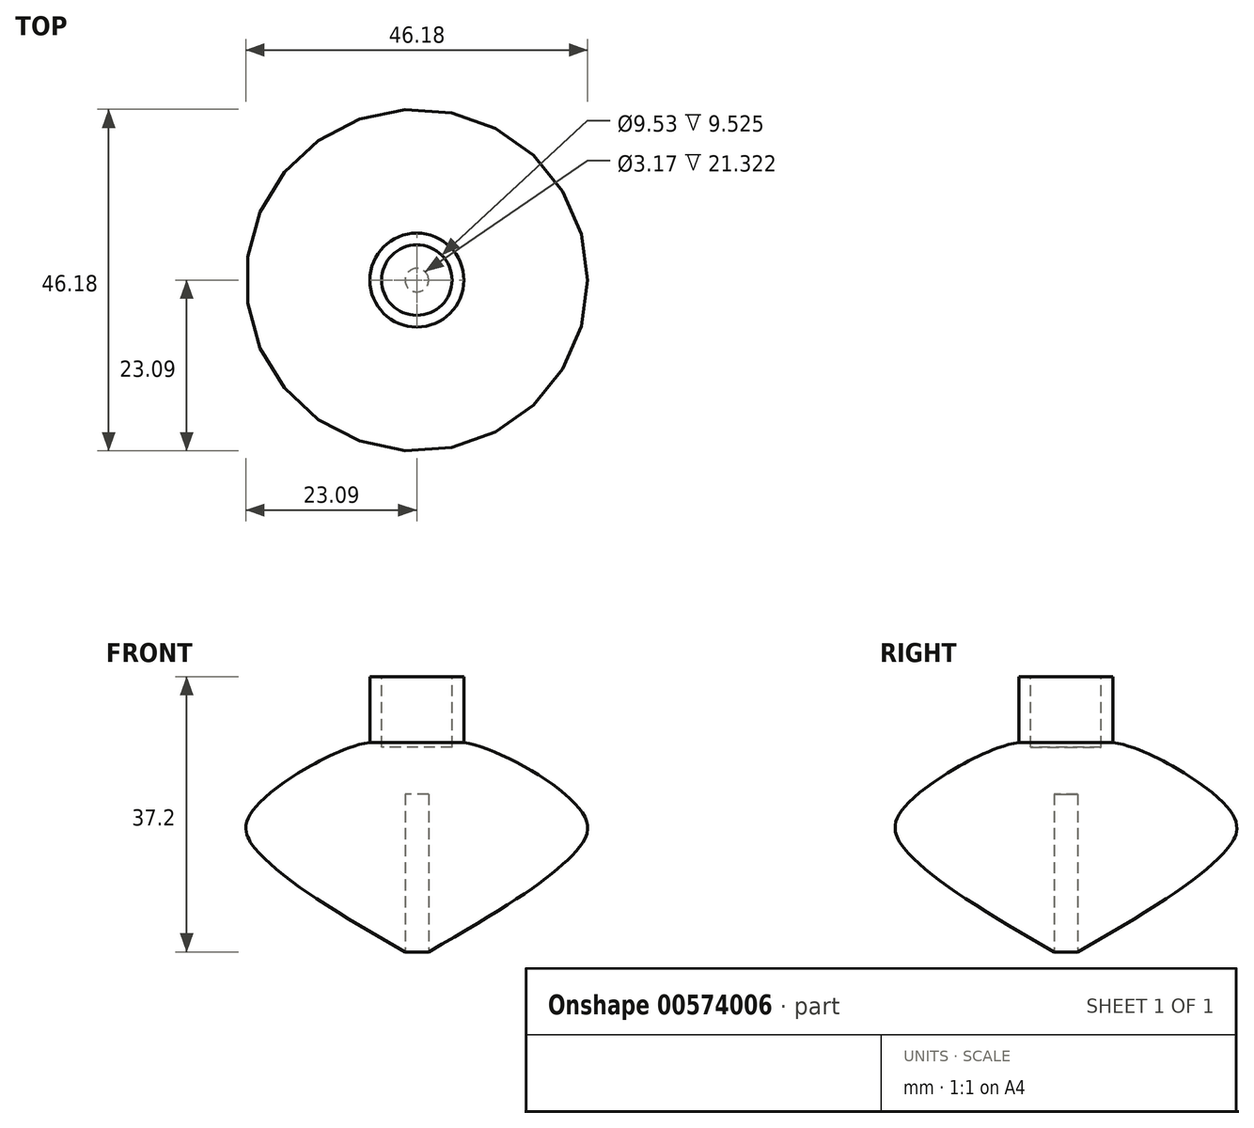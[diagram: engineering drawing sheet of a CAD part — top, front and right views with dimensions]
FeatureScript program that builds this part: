
annotation { "Feature Type Name" : "Feature", "Feature Type Description" : "" }
export const myFeature = defineFeature(function(context is Context, id is Id, definition is map)
    precondition{}
    {
        {
            var Q0;
            Q0=qCreatedBy(makeId("Front.planeOp"),FACE);
            var sketch = newSketch(context, id + "F0", { "sketchPlane" : qUnion([Q0])});
            skFitSpline(sketch, "E0", {"points": [v(0, 0) * mm, v(21.22, 14.16) * mm, v(22.56, 19.42) * mm, v(6.35, 29.21) * mm], "startDerivative": vector(81.94, 46.46) * mm, "endDerivative": vector(-34.66, 4.34) * mm});
            skLineSegment(sketch, "E1", {"start": v(6.35, 29.21) * mm, "end": v(6.35, 38.1) * mm});
            skLineSegment(sketch, "E2", {"start": v(6.35, 38.1) * mm, "end": v(0, 38.1) * mm});
            skLineSegment(sketch, "E3", {"start": v(0, 38.1) * mm, "end": v(0, 0) * mm});
            skLineSegment(sketch, "E4", {"start": v(23.08, 17.5) * mm, "end": v(23.08, 9.82) * mm});
            skSolve(sketch);
        }
        {
            var Q0;
            Q0=qSketchRegion(id+"F0",true);
            var Q1;
            Q1=sQuery(id+"F0.wireOp",EDGE,"E3");
            revolve(context, id + "F1", {"entities" : qUnion([Q0]), "axis" : qUnion([Q1]), "revolveType" : RevolveType.FULL});
        }
        {
            var Q0;
            Q0=makeQuery(id+"F1.opRevolve","SWEPT_FACE",FACE,{"disambiguationData":[OSD([sQuery(id+"F0.wireOp",EDGE,"E2")])]});
            var sketch = newSketch(context, id + "F2", { "sketchPlane" : qUnion([Q0])});
            skCircle(sketch, "E5", {"center": v(0, 0) * mm, "radius": 4.76 * mm});
            skSolve(sketch);
        }
        {
            var Q0;
            Q0=qSketchRegion(id+"F2",true);
            extrude(context, id + "F3", {"entities" : qUnion([Q0]), "operationType" : NewBodyOperationType.REMOVE, "oppositeDirection" : true, "depth" : 9.52 * mm});
        }
        {
            var Q0;
            Q0=qCreatedBy(makeId("Top.planeOp"),FACE);
            var sketch = newSketch(context, id + "F4", { "sketchPlane" : qUnion([Q0])});
            skCircle(sketch, "E6", {"center": v(0, 0) * mm, "radius": 1.59 * mm});
            skSolve(sketch);
        }
        {
            var Q0;
            Q0=qSketchRegion(id+"F4",true);
            extrude(context, id + "F5", {"entities" : qUnion([Q0]), "operationType" : NewBodyOperationType.REMOVE, "depth" : 22.22 * mm});
        }
    });
